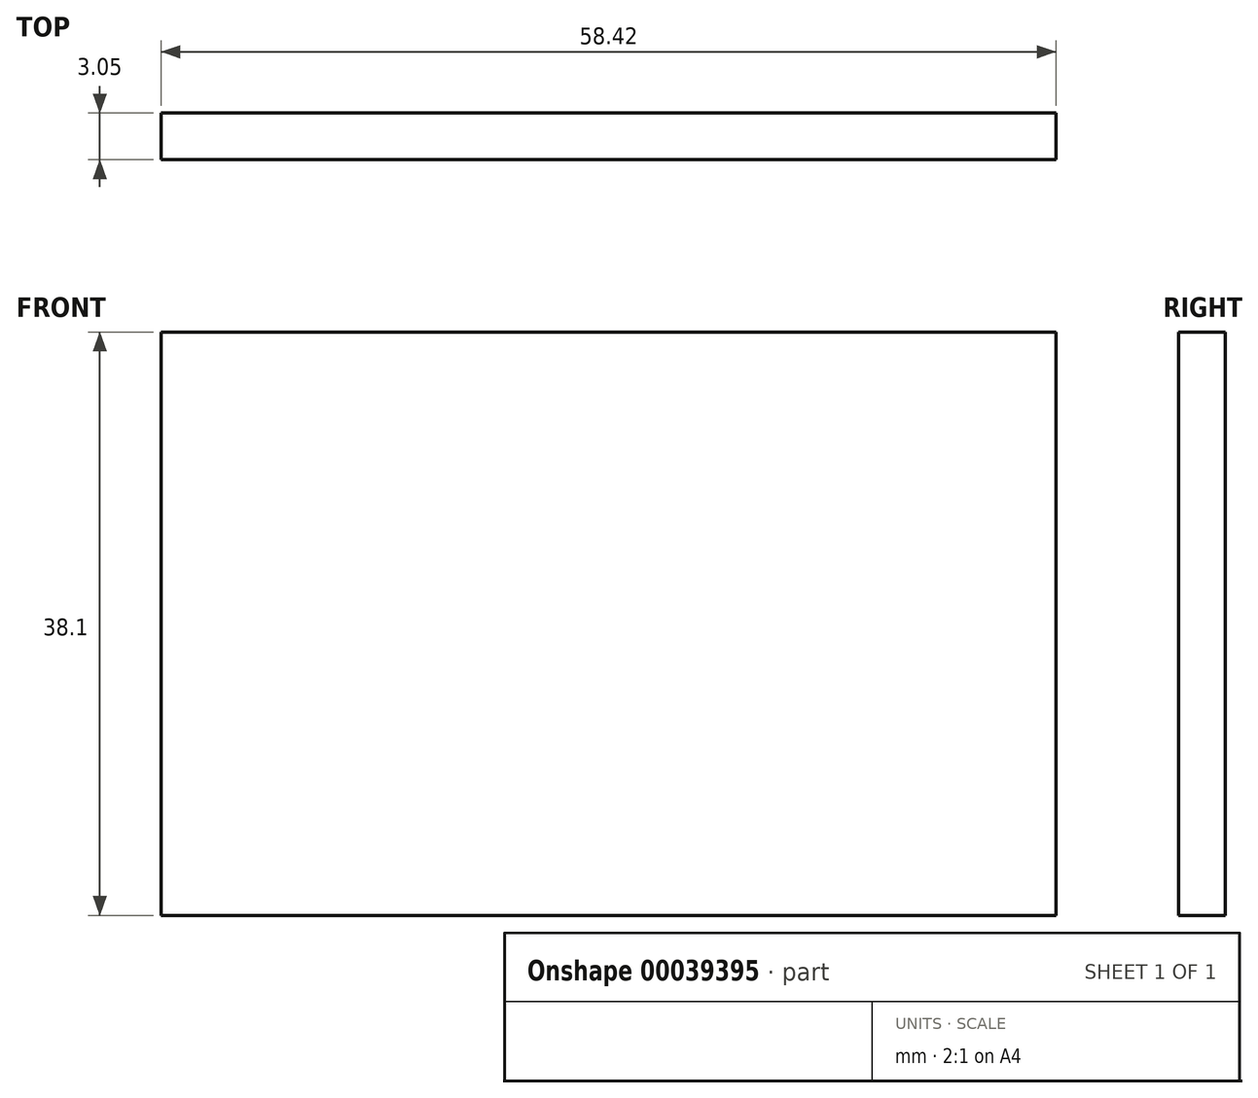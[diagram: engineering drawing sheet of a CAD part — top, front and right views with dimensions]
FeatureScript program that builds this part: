
annotation { "Feature Type Name" : "Feature", "Feature Type Description" : "" }
export const myFeature = defineFeature(function(context is Context, id is Id, definition is map)
    precondition{}
    {
        {
            var Q0;
            Q0=qCreatedBy(makeId("Front.planeOp"),FACE);
            var sketch = newSketch(context, id + "F0", { "sketchPlane" : qUnion([Q0])});
            skLineSegment(sketch, "E0.bottom", {"start": v(0, 0) * mm, "end": v(58.42, 0) * mm});
            skLineSegment(sketch, "E0.top", {"start": v(0, 38.1) * mm, "end": v(58.42, 38.1) * mm});
            skLineSegment(sketch, "E0.left", {"start": v(0, 0) * mm, "end": v(0, 38.1) * mm});
            skLineSegment(sketch, "E0.right", {"start": v(58.42, 0) * mm, "end": v(58.42, 38.1) * mm});
            skSolve(sketch);
        }
        {
            var Q0;
            Q0 = qSketchRegion(id + "F0", true);
            extrude(context, id + "F1", {"entities" : qUnion([Q0]), "depth" : 3.05 * mm});
        }
    });
